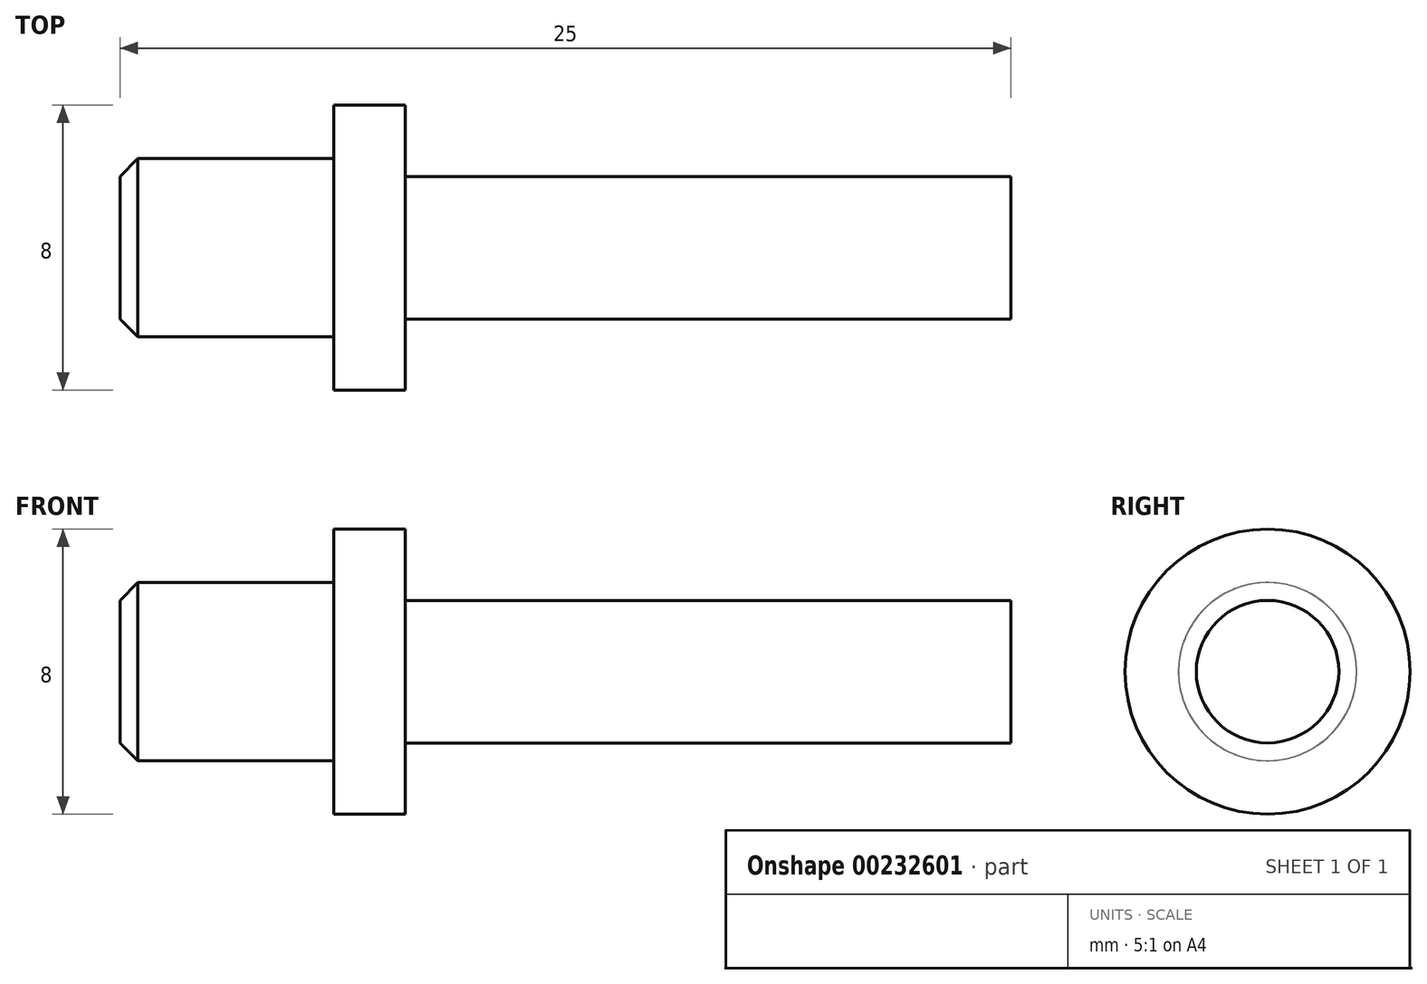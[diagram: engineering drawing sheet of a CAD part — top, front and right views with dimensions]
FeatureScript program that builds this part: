
annotation { "Feature Type Name" : "Feature", "Feature Type Description" : "" }
export const myFeature = defineFeature(function(context is Context, id is Id, definition is map)
    precondition{}
    {
        {
            var Q0;
            Q0=qCreatedBy(makeId("Front.planeOp"),FACE);
            var sketch = newSketch(context, id + "F0", { "sketchPlane" : qUnion([Q0])});
            skLineSegment(sketch, "E0", {"start": v(0, 0) * mm, "end": v(25, 0) * mm});
            skLineSegment(sketch, "E1", {"start": v(25, 0) * mm, "end": v(25, 2) * mm});
            skLineSegment(sketch, "E2", {"start": v(25, 2) * mm, "end": v(8, 2) * mm});
            skLineSegment(sketch, "E3", {"start": v(8, 2) * mm, "end": v(8, 4) * mm});
            skLineSegment(sketch, "E4", {"start": v(8, 4) * mm, "end": v(6, 4) * mm});
            skLineSegment(sketch, "E5", {"start": v(6, 4) * mm, "end": v(6, 2.5) * mm});
            skLineSegment(sketch, "E6", {"start": v(6, 2.5) * mm, "end": v(0, 2.5) * mm});
            skLineSegment(sketch, "E7", {"start": v(0, 2.5) * mm, "end": v(0, 0) * mm});
            skSolve(sketch);
        }
        {
            var Q0;
            Q0 = qSketchRegion(id + "F0", true);
            var Q1;
            Q1=sQuery(id+"F0.wireOp",EDGE,"E0");
            revolve(context, id + "F1", {"entities" : qUnion([Q0]), "axis" : qUnion([Q1]), "revolveType" : RevolveType.FULL});
        }
        {
            var Q0;
            Q0=makeQuery(id+"F1.opRevolve","SWEPT_EDGE",EDGE,{"disambiguationData":[OSD([sQuery(id+"F0.wireOp",EDGE,"E6"),sQuery(id+"F0.wireOp",EDGE,"E7")])]});
            chamfer(context, id + "F2", {"entities" : qUnion([Q0]), "width" : .5 * mm, "tangentPropagation" : true});
        }
    });
